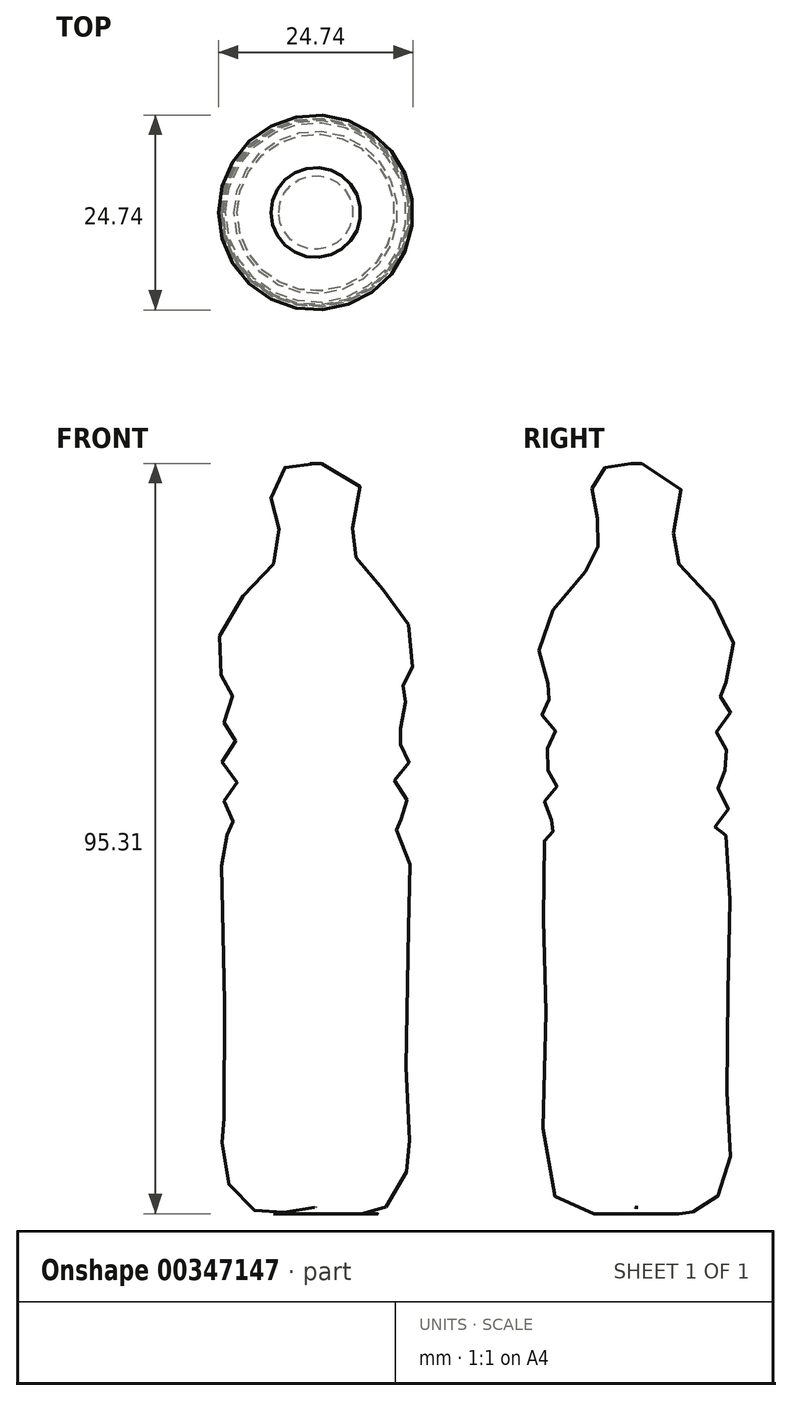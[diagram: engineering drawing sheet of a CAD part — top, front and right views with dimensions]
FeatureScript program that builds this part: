
annotation { "Feature Type Name" : "Feature", "Feature Type Description" : "" }
export const myFeature = defineFeature(function(context is Context, id is Id, definition is map)
    precondition{}
    {
        {
            var Q0;
            Q0=qCreatedBy(makeId("Front.planeOp"),FACE);
            var sketch = newSketch(context, id + "F0", { "sketchPlane" : qUnion([Q0])});
            skLineSegment(sketch, "E0", {"start": v(0, 0) * mm, "end": v(0, -96.44) * mm});
            skFitSpline(sketch, "E1", {"points": [v(0, -95.08) * mm, v(-2.16, -95.21) * mm, v(-4.22, -95.74) * mm, v(-6.34, -95.78) * mm, v(-8.27, -95.28) * mm, v(-10.26, -93.79) * mm, v(-11.98, -87.91) * mm, v(-11.88, -86.65) * mm, v(-12.02, -84.9) * mm, v(-11.65, -83.5) * mm, v(-11.95, -49.93) * mm, v(-11.75, -48.64) * mm, v(-11.25, -47.7) * mm, v(-10.3, -47.11) * mm, v(-10, -46.55) * mm, v(-10.79, -45.82) * mm, v(-11.58, -44.69) * mm, v(-11.68, -43.6) * mm, v(-10.89, -42.3) * mm, v(-10.1, -41.57) * mm, v(-10.1, -40.7) * mm, v(-11.25, -39.55) * mm, v(-11.88, -38.19) * mm, v(-10.92, -36.36) * mm, v(-10.22, -35.9) * mm, v(-10.02, -34.87) * mm, v(-11.09, -33.97) * mm, v(-11.98, -32.32) * mm, v(-10.85, -30.3) * mm, v(-10.36, -29.86) * mm, v(-11.48, -28.24) * mm, v(-12.21, -26.68) * mm, v(-12.25, -22.66) * mm, v(-10.79, -19.41) * mm, v(-5.98, -13.8) * mm, v(-5.35, -13.24) * mm, v(-4.95, -11.48) * mm, v(-4.82, -7.73) * mm, v(-5.38, -7.04) * mm, v(-5.38, -2.03) * mm, v(-4.22, -1.13) * mm, v(-1.33, -0.57) * mm, v(0, -0.57) * mm], "startDerivative": vector(-91.4, 0.11) * mm, "endDerivative": vector(61.24, -4.52) * mm});
            skSolve(sketch);
        }
        {
            var Q0;
            {var subQ0=sQuery(id+"F0.wireOp",EDGE,"E1");Q0=makeQuery(id+"F0.imprint","IMPRINT",FACE,{"disambiguationData":[TD([[makeQuery(id+"F0.imprint","IMPRINT",EDGE,{"derivedFrom":subQ0}),-1.0]])]});}
            var Q1;
            Q1=sQuery(id+"F0.wireOp",EDGE,"E0");
            revolve(context, id + "F1", {"entities" : qUnion([Q0]), "axis" : qUnion([Q1]), "revolveType" : RevolveType.FULL});
        }
    });
